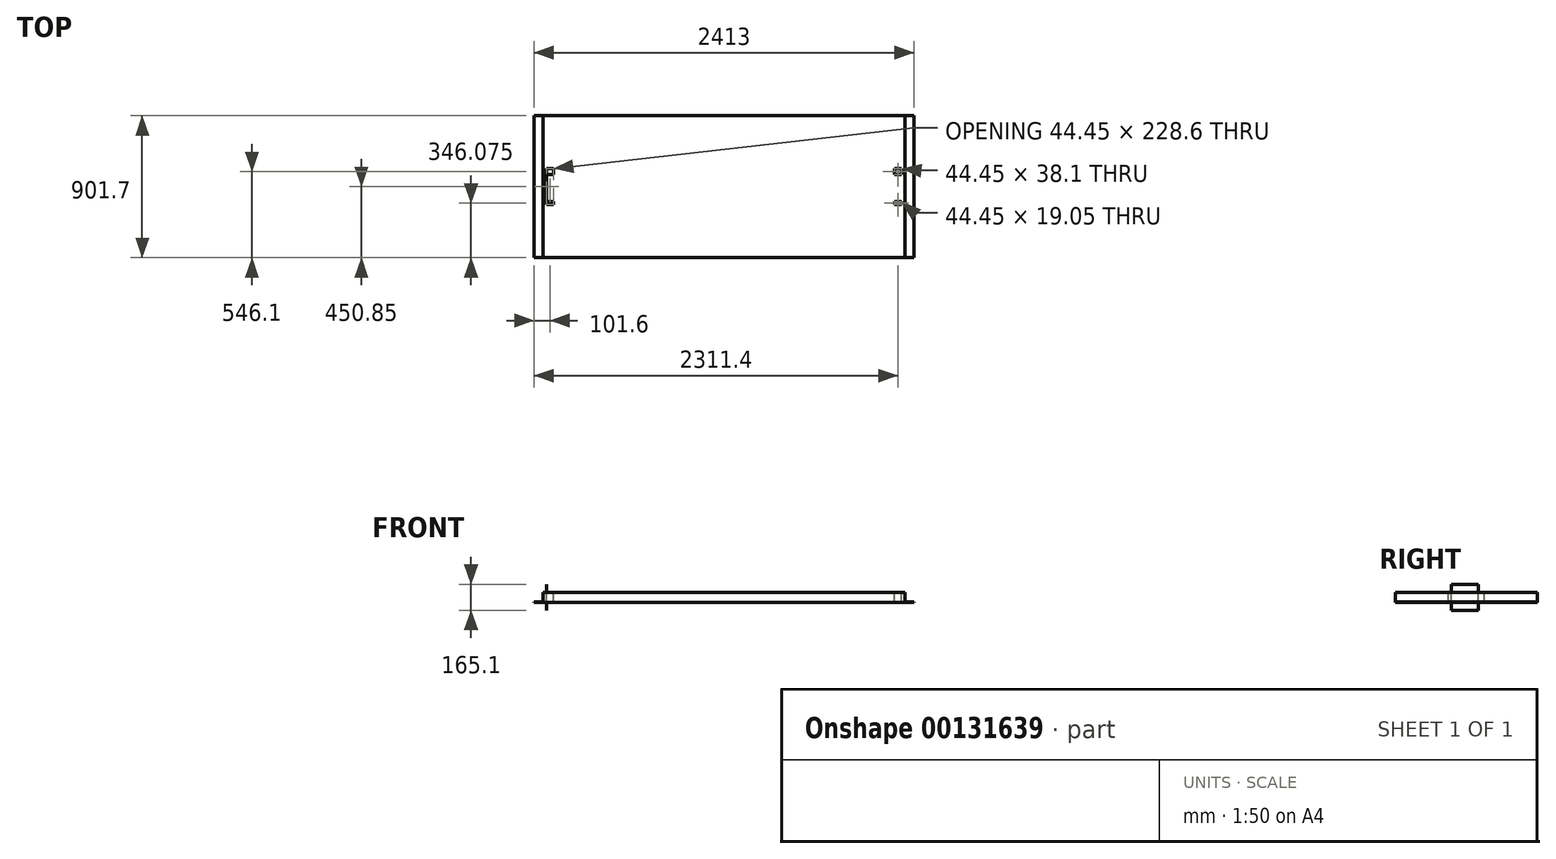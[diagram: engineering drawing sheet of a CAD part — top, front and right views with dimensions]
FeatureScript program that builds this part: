
annotation { "Feature Type Name" : "Feature", "Feature Type Description" : "" }
export const myFeature = defineFeature(function(context is Context, id is Id, definition is map)
    precondition{}
    {
        {
            var Q0;
            Q0=qCreatedBy(makeId("Top.planeOp"),FACE);
            var sketch = newSketch(context, id + "F0", { "sketchPlane" : qUnion([Q0])});
            skLineSegment(sketch, "E0.bottom", {"start": v(1149.35, 450.85) * mm, "end": v(-1149.35, 450.85) * mm});
            skLineSegment(sketch, "E0.top", {"start": v(1149.35, -450.85) * mm, "end": v(-1149.35, -450.85) * mm});
            skLineSegment(sketch, "E0.left", {"start": v(1149.35, 450.85) * mm, "end": v(1149.35, -450.85) * mm});
            skLineSegment(sketch, "E0.right", {"start": v(-1149.35, 450.85) * mm, "end": v(-1149.35, -450.85) * mm});
            skPoint(sketch, "E0.middle", {"position": v(0, 0) * mm});
            skSolve(sketch);
        }
        {
            var Q0;
            Q0 = qSketchRegion(id + "F0", true);
            extrude(context, id + "F1", {"entities" : qUnion([Q0]), "depth" : 63.5 * mm});
        }
        {
            var Q0;
            Q0=makeQuery(id+"F1.opExtrude","CAP_FACE",FACE,{"disambiguationData":[OSD([sQuery(id+"F0.wireOp",EDGE,"E0.bottom"),sQuery(id+"F0.wireOp",EDGE,"E0.top"),sQuery(id+"F0.wireOp",EDGE,"E0.left"),sQuery(id+"F0.wireOp",EDGE,"E0.right")])],"isStart":true});
            var sketch = newSketch(context, id + "F2", { "sketchPlane" : qUnion([Q0])});
            skLineSegment(sketch, "E1.bottom", {"start": v(-1149.35, -450.85) * mm, "end": v(-1206.5, -450.85) * mm});
            skLineSegment(sketch, "E1.top", {"start": v(-1149.35, 450.85) * mm, "end": v(-1206.5, 450.85) * mm});
            skLineSegment(sketch, "E1.left", {"start": v(-1149.35, -450.85) * mm, "end": v(-1149.35, 450.85) * mm});
            skLineSegment(sketch, "E1.right", {"start": v(-1206.5, -450.85) * mm, "end": v(-1206.5, 450.85) * mm});
            skLineSegment(sketch, "E2.MirrorCS", {"start": v(1149.35, -450.85) * mm, "end": v(1206.5, -450.85) * mm});
            skLineSegment(sketch, "E3.MirrorCS", {"start": v(1206.5, -450.85) * mm, "end": v(1206.5, 450.85) * mm});
            skLineSegment(sketch, "E4.MirrorCS", {"start": v(1149.35, 450.85) * mm, "end": v(1206.5, 450.85) * mm});
            skLineSegment(sketch, "E5.MirrorCS", {"start": v(1149.35, -450.85) * mm, "end": v(1149.35, 450.85) * mm});
            skSolve(sketch);
        }
        {
            var Q0;
            Q0 = qSketchRegion(id + "F2", true);
            extrude(context, id + "F3", {"entities" : qUnion([Q0]), "operationType" : NewBodyOperationType.ADD, "oppositeDirection" : true, "depth" : 1.98 * mm});
        }
        {
            var Q0;
            Q0=qCreatedBy(makeId("Top.planeOp"),FACE);
            var sketch = newSketch(context, id + "F4", { "sketchPlane" : qUnion([Q0])});
            skLineSegment(sketch, "E6.bottom", {"start": v(1127.12, -114.3) * mm, "end": v(-1127.13, -114.3) * mm});
            skLineSegment(sketch, "E6.top", {"start": v(1127.13, 114.3) * mm, "end": v(-1127.13, 114.3) * mm});
            skLineSegment(sketch, "E6.left", {"start": v(1127.13, -114.3) * mm, "end": v(1127.13, 114.3) * mm});
            skLineSegment(sketch, "E6.right", {"start": v(-1127.13, -114.3) * mm, "end": v(-1127.13, 114.3) * mm});
            skPoint(sketch, "E6.middle", {"position": v(0, 0) * mm});
            skSolve(sketch);
        }
        {
            var Q0;
            Q0 = qSketchRegion(id + "F4", true);
            extrude(context, id + "F5", {"entities" : qUnion([Q0]), "depth" : 63.5 * mm});
        }
        {
            var Q0;
            Q0=makeQuery(id+"F5.opExtrude","CAP_FACE",FACE,{"disambiguationData":[OSD([sQuery(id+"F4.wireOp",EDGE,"E6.bottom"),sQuery(id+"F4.wireOp",EDGE,"E6.top"),sQuery(id+"F4.wireOp",EDGE,"E6.left"),sQuery(id+"F4.wireOp",EDGE,"E6.right")])],"isStart":false});
            var sketch = newSketch(context, id + "F6", { "sketchPlane" : qUnion([Q0])});
            skLineSegment(sketch, "E7.bottom", {"start": v(-1127.13, 114.3) * mm, "end": v(-1082.68, 114.3) * mm});
            skLineSegment(sketch, "E7.top", {"start": v(-1127.13, 76.2) * mm, "end": v(-1082.68, 76.2) * mm});
            skLineSegment(sketch, "E7.left", {"start": v(-1127.13, 114.3) * mm, "end": v(-1127.13, 76.2) * mm});
            skLineSegment(sketch, "E7.right", {"start": v(-1082.68, 114.3) * mm, "end": v(-1082.68, 76.2) * mm});
            skLineSegment(sketch, "E8.bottom", {"start": v(-1127.13, -114.3) * mm, "end": v(-1082.68, -114.3) * mm});
            skLineSegment(sketch, "E8.top", {"start": v(-1127.13, -95.25) * mm, "end": v(-1082.68, -95.25) * mm});
            skLineSegment(sketch, "E8.left", {"start": v(-1127.13, -114.3) * mm, "end": v(-1127.13, -95.25) * mm});
            skLineSegment(sketch, "E8.right", {"start": v(-1082.68, -114.3) * mm, "end": v(-1082.68, -95.25) * mm});
            skLineSegment(sketch, "E9.MirrorCS", {"start": v(1082.68, -114.3) * mm, "end": v(1082.68, -95.25) * mm});
            skLineSegment(sketch, "E10.MirrorCS", {"start": v(1127.13, -114.3) * mm, "end": v(1127.13, -95.25) * mm});
            skLineSegment(sketch, "E11.MirrorCS", {"start": v(1127.13, -95.25) * mm, "end": v(1082.68, -95.25) * mm});
            skLineSegment(sketch, "E12.MirrorCS", {"start": v(1127.13, -114.3) * mm, "end": v(1082.68, -114.3) * mm});
            skLineSegment(sketch, "E13.MirrorCS", {"start": v(1082.68, 114.3) * mm, "end": v(1082.68, 76.2) * mm});
            skLineSegment(sketch, "E14.MirrorCS", {"start": v(1127.13, 114.3) * mm, "end": v(1127.13, 76.2) * mm});
            skLineSegment(sketch, "E15.MirrorCS", {"start": v(1127.13, 114.3) * mm, "end": v(1082.68, 114.3) * mm});
            skLineSegment(sketch, "E16.MirrorCS", {"start": v(1127.13, 76.2) * mm, "end": v(1082.68, 76.2) * mm});
            skSolve(sketch);
        }
        {
            var Q0;
            Q0 = qSketchRegion(id + "F6", true);
            extrude(context, id + "F7", {"entities" : qUnion([Q0]), "operationType" : NewBodyOperationType.REMOVE, "endBound" : BoundingType.THROUGH_ALL, "oppositeDirection" : true, "depth" : 25.4 * mm});
        }
        {
            var Q0;
            Q0=makeQuery(id+"F5.opExtrude","SWEPT_FACE",FACE,{"disambiguationData":[OSD([sQuery(id+"F4.wireOp",EDGE,"E6.right")])]});
            var sketch = newSketch(context, id + "F8", { "sketchPlane" : qUnion([Q0])});
            skLineSegment(sketch, "E17", {"start": v(-76.2, 31.75) * mm, "end": v(-76.2, 114.3) * mm});
            skLineSegment(sketch, "E18", {"start": v(-76.2, 114.3) * mm, "end": v(95.25, 114.3) * mm});
            skPoint(sketch, "E18.endSnap0", {"position": v(95.25, 31.75) * mm});
            skLineSegment(sketch, "E19", {"start": v(95.25, 114.3) * mm, "end": v(95.25, 31.75) * mm});
            skLineSegment(sketch, "E20", {"start": v(-76.2, 31.75) * mm, "end": v(95.25, 31.75) * mm, "construction": true});
            skLineSegment(sketch, "E21.MirrorCS", {"start": v(-76.2, 31.75) * mm, "end": v(-76.2, -50.8) * mm});
            skLineSegment(sketch, "E22.MirrorCS", {"start": v(-76.2, -50.8) * mm, "end": v(95.25, -50.8) * mm});
            skLineSegment(sketch, "E23.MirrorCS", {"start": v(95.25, -50.8) * mm, "end": v(95.25, 31.75) * mm});
            skSolve(sketch);
        }
        {
            var Q0;
            Q0 = qSketchRegion(id + "F8", true);
            extrude(context, id + "F9", {"entities" : qUnion([Q0]), "operationType" : NewBodyOperationType.ADD, "oppositeDirection" : true, "depth" : 1.59 * mm});
        }
    });
